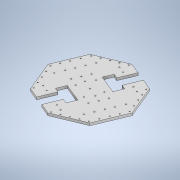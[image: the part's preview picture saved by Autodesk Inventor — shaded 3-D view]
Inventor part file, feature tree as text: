
AUTODESK INVENTOR PART (.ipt)
format: ipt  version: 2020 (Build 240168000, 168)  size: 338,432 bytes
history: native  units: mm
features: extrude x2, sketch x2
ambient origin geometry x8: Origin, YZ Plane, XZ Plane, XY Plane, X Axis, Y Axis, Z Axis, Center Point
bodies: Solide1 (feature_tree)
feature tree (4):
  extrude  "Extrusion1"  Depth=10.0mm TaperAngle=0.0deg
  extrude  "Extrusion2"  Depth=4.5mm
  sketch  "Esquisse1"
  sketch  "Esquisse2"
